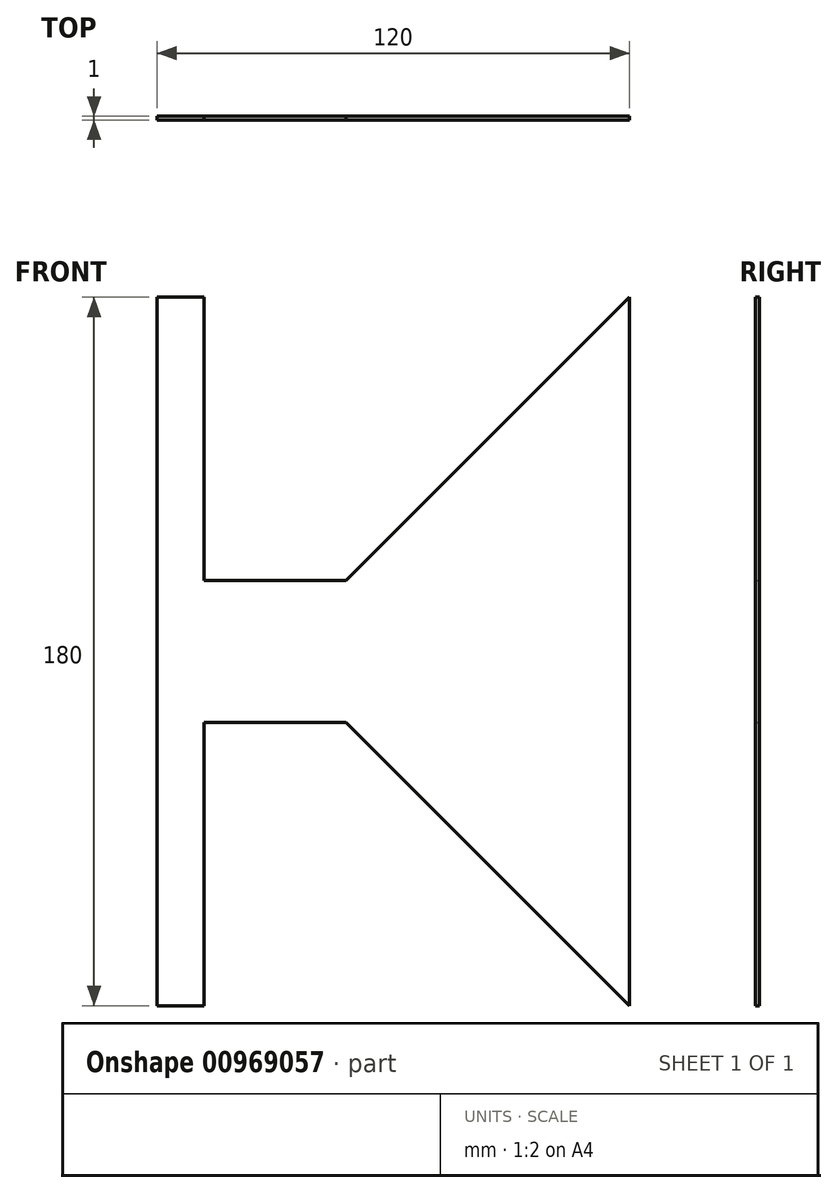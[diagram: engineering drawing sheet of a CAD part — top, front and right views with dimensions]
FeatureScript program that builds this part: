
annotation { "Feature Type Name" : "Feature", "Feature Type Description" : "" }
export const myFeature = defineFeature(function(context is Context, id is Id, definition is map)
    precondition{}
    {
        {
            var Q0;
            Q0=qCreatedBy(makeId("Front.planeOp"),FACE);
            var sketch = newSketch(context, id + "F0", { "sketchPlane" : qUnion([Q0])});
            skLineSegment(sketch, "E0.bottom", {"start": v(0, 90) * mm, "end": v(12, 90) * mm});
            skLineSegment(sketch, "E0.top", {"start": v(0, -90) * mm, "end": v(12, -90) * mm});
            skLineSegment(sketch, "E0.left", {"start": v(0, 90) * mm, "end": v(0, -90) * mm});
            skLineSegment(sketch, "E0.right", {"start": v(12, 90) * mm, "end": v(12, 18) * mm});
            skLineSegment(sketch, "E1.bottom", {"start": v(12, 18) * mm, "end": v(48, 18) * mm});
            skLineSegment(sketch, "E1.top", {"start": v(12, -18) * mm, "end": v(48, -18) * mm});
            skLineSegment(sketch, "E2", {"start": v(48, 18) * mm, "end": v(120, 90) * mm});
            skLineSegment(sketch, "E3", {"start": v(48, -18) * mm, "end": v(120, -90) * mm});
            skLineSegment(sketch, "E4", {"start": v(120, 90) * mm, "end": v(120, -90) * mm});
            skLineSegment(sketch, "E5.trimOffspring", {"start": v(12, -18) * mm, "end": v(12, -90) * mm});
            skSolve(sketch);
        }
        {
            var Q0;
            Q0 = qSketchRegion(id + "F0", true);
            extrude(context, id + "F1", {"entities" : qUnion([Q0]), "depth" : 1 * mm, "offsetDistance" : 25 * mm});
        }
    });
